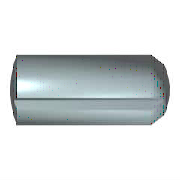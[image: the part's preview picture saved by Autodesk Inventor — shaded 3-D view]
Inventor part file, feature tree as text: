
AUTODESK INVENTOR PART (.ipt)
format: ipt  version: 2021 (Build 250183000, 183)  size: 145,920 bytes
history: native  units: mm (DEFAULTED — no unit token found)
features: sketch x2, extrude x1, pattern_circular x1
ambient origin geometry x8: Origin, YZ Plane, XZ Plane, XY Plane, X Axis, Y Axis, Z Axis, Center Point
bodies: Solid1 (feature_tree), Body (feature_tree)
feature tree (4):
  extrude  "Groove"  Depth=20.0mm
  pattern_circular  "Grooves"  Angle=15.0deg  [1 undecoded]
  sketch  "Sketch1"  dims[d0=90.0mm d1=20.0mm]
  sketch  "Sketch2"  dims[d2=5.2mm d3=15.0deg d4=2.5mm d5=2.5mm d9=90.0deg d6=6.108652mm d7=6.108652mm d8=1.0mm d15=10.0mm d10=0.0mm d11=30.0mm d12=360.0deg d13=-2.5mm d28=2.5mm d29=0.0mm]
note: 1 required parameter value undecoded (feature->parameter linkage not recoverable at this tier; creation-order binding heuristic only, values carry confidence <= 0.55)
